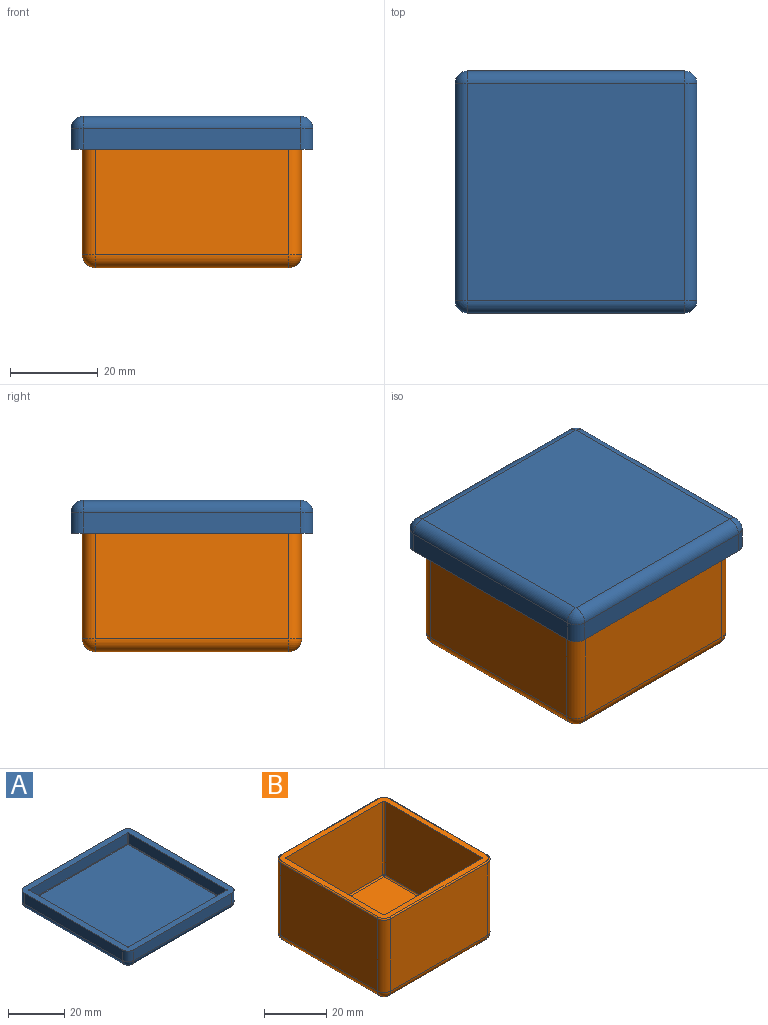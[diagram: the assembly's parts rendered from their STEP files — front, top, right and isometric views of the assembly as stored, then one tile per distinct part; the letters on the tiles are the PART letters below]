
ASSEMBLY  parts=2 mates=1
PART A: 35 faces, bbox 55.1x55.1x7.5 mm
  f0: plane 55.1x55.1mm, normal (0,0,1), area 519.3mm2, adj f1,f2,f3,f4,f6,f8,f11,f17
  f1: plane 49.5x4.7mm, normal (-1,0,0), area 232.7mm2, adj f0,f11,f15,f17
  f2: plane 49.5x4.7mm, normal (0,-1,0), area 232.7mm2, adj f0,f8,f14,f17
  f3: plane 49.5x4.7mm, normal (1,0,0), area 232.7mm2, adj f0,f6,f8,f9
  f4: plane 49.5x4.7mm, normal (0,1,0), area 232.7mm2, adj f0,f6,f10,f11
  f5: plane 49.5x49.5mm, normal (0,0,-1), area 2450.2mm2, adj f9,f10,f14,f15
  f6: cylinder r=2.8mm len=4.7mm, axis (0,0,1), area 20.7mm2, adj f0,f3,f4,f7
  f7: sphere r=2.8mm, area 12.3mm2, adj f6,f9,f10
  f8: cylinder r=2.8mm len=4.7mm, axis (0,0,-1), area 20.7mm2, adj f0,f2,f3,f12
  f9: cylinder r=2.8mm len=49.5mm, axis (0,1,0), area 217.7mm2, adj f3,f5,f7,f12
  f10: cylinder r=2.8mm len=49.5mm, axis (-1,0,0), area 217.7mm2, adj f4,f5,f7,f13
  f11: cylinder r=2.8mm len=4.7mm, axis (0,0,-1), area 20.7mm2, adj f0,f1,f4,f13
  f12: sphere r=2.8mm, area 12.3mm2, adj f8,f9,f14
  f13: sphere r=2.8mm, area 12.3mm2, adj f10,f11,f15
  f14: cylinder r=2.8mm len=49.5mm, axis (1,0,0), area 217.7mm2, adj f2,f5,f12,f16
  f15: cylinder r=2.8mm len=49.5mm, axis (0,-1,0), area 217.7mm2, adj f1,f5,f13,f16
  f16: sphere r=2.8mm, area 12.3mm2, adj f14,f15,f17
  f17: cylinder r=2.8mm len=4.7mm, axis (0,0,1), area 20.7mm2, adj f0,f1,f2,f16
  f18: plane 49.5x4.7mm, normal (1,0,0), area 232.7mm2, adj f0,f28,f32,f34
  f19: plane 49.5x4.7mm, normal (0,1,0), area 232.7mm2, adj f0,f25,f31,f34
  f20: plane 49.5x4.7mm, normal (-1,0,0), area 232.7mm2, adj f0,f23,f25,f26
  f21: plane 49.5x4.7mm, normal (0,-1,0), area 232.7mm2, adj f0,f23,f27,f28
  f22: plane 49.5x49.5mm, normal (0,0,1), area 2450.2mm2, adj f26,f27,f31,f32
  f23: cylinder r=0.3mm len=4.7mm, axis (0,0,1), area 2.2mm2, adj f0,f20,f21,f24
  f24: sphere r=0.3mm, area 0.1mm2, adj f23,f26,f27
  f25: cylinder r=0.3mm len=4.7mm, axis (0,0,-1), area 2.2mm2, adj f0,f19,f20,f29
  f26: cylinder r=0.3mm len=49.5mm, axis (0,1,0), area 23.3mm2, adj f20,f22,f24,f29
  f27: cylinder r=0.3mm len=49.5mm, axis (-1,0,0), area 23.3mm2, adj f21,f22,f24,f30
  f28: cylinder r=0.3mm len=4.7mm, axis (0,0,-1), area 2.2mm2, adj f0,f18,f21,f30
  f29: sphere r=0.3mm, area 0.1mm2, adj f25,f26,f31
  f30: sphere r=0.3mm, area 0.1mm2, adj f27,f28,f32
  f31: cylinder r=0.3mm len=49.5mm, axis (1,0,0), area 23.3mm2, adj f19,f22,f29,f33
  f32: cylinder r=0.3mm len=49.5mm, axis (0,-1,0), area 23.3mm2, adj f18,f22,f30,f33
  f33: sphere r=0.3mm, area 0.1mm2, adj f31,f32,f34
  f34: cylinder r=0.3mm len=4.7mm, axis (0,0,1), area 2.2mm2, adj f0,f18,f19,f33
PART B: 43 faces, bbox 50.5x50.5x32 mm
  f0: plane 49.1x49.1mm, normal (0,0,1), area 380.4mm2, adj f18,f19,f20,f21,f23,f25,f28,f34
  f1: plane 44x28.55mm, normal (-1,0,0), area 1256.2mm2, adj f11,f15,f17,f42
  f2: plane 44x28.55mm, normal (0,-1,0), area 1256.2mm2, adj f8,f14,f17,f38
  f3: plane 44x28.55mm, normal (1,0,0), area 1256.2mm2, adj f6,f8,f9,f35
  f4: plane 44x28.55mm, normal (0,1,0), area 1256.2mm2, adj f6,f10,f11,f39
  f5: plane 44x44mm, normal (0,0,-1), area 1936mm2, adj f9,f10,f14,f15
  f6: cylinder r=3mm len=28.55mm, axis (0,0,1), area 134.5mm2, adj f3,f4,f7,f37
  f7: sphere r=3mm, area 14.1mm2, adj f6,f9,f10
  f8: cylinder r=3mm len=28.55mm, axis (0,0,-1), area 134.5mm2, adj f2,f3,f12,f36
  f9: cylinder r=3mm len=44mm, axis (0,1,0), area 207.3mm2, adj f3,f5,f7,f12
  f10: cylinder r=3mm len=44mm, axis (-1,0,0), area 207.3mm2, adj f4,f5,f7,f13
  f11: cylinder r=3mm len=28.55mm, axis (0,0,-1), area 134.5mm2, adj f1,f4,f13,f41
  f12: sphere r=3mm, area 14.1mm2, adj f8,f9,f14
  f13: sphere r=3mm, area 14.1mm2, adj f10,f11,f15
  f14: cylinder r=3mm len=44mm, axis (1,0,0), area 207.3mm2, adj f2,f5,f12,f16
  f15: cylinder r=3mm len=44mm, axis (0,-1,0), area 207.3mm2, adj f1,f5,f13,f16
  f16: sphere r=3mm, area 14.1mm2, adj f14,f15,f17
  f17: cylinder r=3mm len=28.55mm, axis (0,0,1), area 134.5mm2, adj f1,f2,f16,f40
  f18: plane 44x29mm, normal (1,0,0), area 1276mm2, adj f0,f28,f32,f34
  f19: plane 44x29mm, normal (0,1,0), area 1276mm2, adj f0,f25,f31,f34
  f20: plane 44x29mm, normal (-1,0,0), area 1276mm2, adj f0,f23,f25,f26
  f21: plane 44x29mm, normal (0,-1,0), area 1276mm2, adj f0,f23,f27,f28
  f22: plane 44x44mm, normal (0,0,1), area 1936mm2, adj f26,f27,f31,f32
  f23: cylinder r=0.5mm len=29mm, axis (0,0,1), area 22.8mm2, adj f0,f20,f21,f24
  f24: sphere r=0.5mm, area 0.4mm2, adj f23,f26,f27
  f25: cylinder r=0.5mm len=29mm, axis (0,0,-1), area 22.8mm2, adj f0,f19,f20,f29
  f26: cylinder r=0.5mm len=44mm, axis (0,1,0), area 34.6mm2, adj f20,f22,f24,f29
  f27: cylinder r=0.5mm len=44mm, axis (-1,0,0), area 34.6mm2, adj f21,f22,f24,f30
  f28: cylinder r=0.5mm len=29mm, axis (0,0,-1), area 22.8mm2, adj f0,f18,f21,f30
  f29: sphere r=0.5mm, area 0.4mm2, adj f25,f26,f31
  f30: sphere r=0.5mm, area 0.4mm2, adj f27,f28,f32
  f31: cylinder r=0.5mm len=44mm, axis (1,0,0), area 34.6mm2, adj f19,f22,f29,f33
  f32: cylinder r=0.5mm len=44mm, axis (0,-1,0), area 34.6mm2, adj f18,f22,f30,f33
  f33: sphere r=0.5mm, area 0.4mm2, adj f31,f32,f34
  f34: cylinder r=0.5mm len=29mm, axis (0,0,1), area 22.8mm2, adj f0,f18,f19,f33
  f35: cylinder r=0.45mm len=44mm, axis (0,-1,0), area 31.1mm2, adj f0,f3,f36,f37
  f36: torus R=2.55mm, axis (0,0,1), area 3.1mm2, adj f0,f8,f35,f38
  f37: torus R=2.55mm, axis (0,0,1), area 3.1mm2, adj f0,f6,f35,f39
  f38: cylinder r=0.45mm len=44mm, axis (-1,0,0), area 31.1mm2, adj f0,f2,f36,f40
  f39: cylinder r=0.45mm len=44mm, axis (1,0,0), area 31.1mm2, adj f0,f4,f37,f41
  f40: torus R=2.55mm, axis (0,0,1), area 3.1mm2, adj f0,f17,f38,f42
  f41: torus R=2.55mm, axis (0,0,1), area 3.1mm2, adj f0,f11,f39,f42
  f42: cylinder r=0.45mm len=44mm, axis (0,1,0), area 31.1mm2, adj f0,f1,f40,f41
PLACE A rot(axis=(0,1,0),180deg) t=(47.56,-0.42,33.46)mm
PLACE B t=(-2.49,-0.37,1.46)mm
MATE planar A.f22 <-> B.f0  axis (0,0,-1) through (22.51,24.63,33.46)mm
